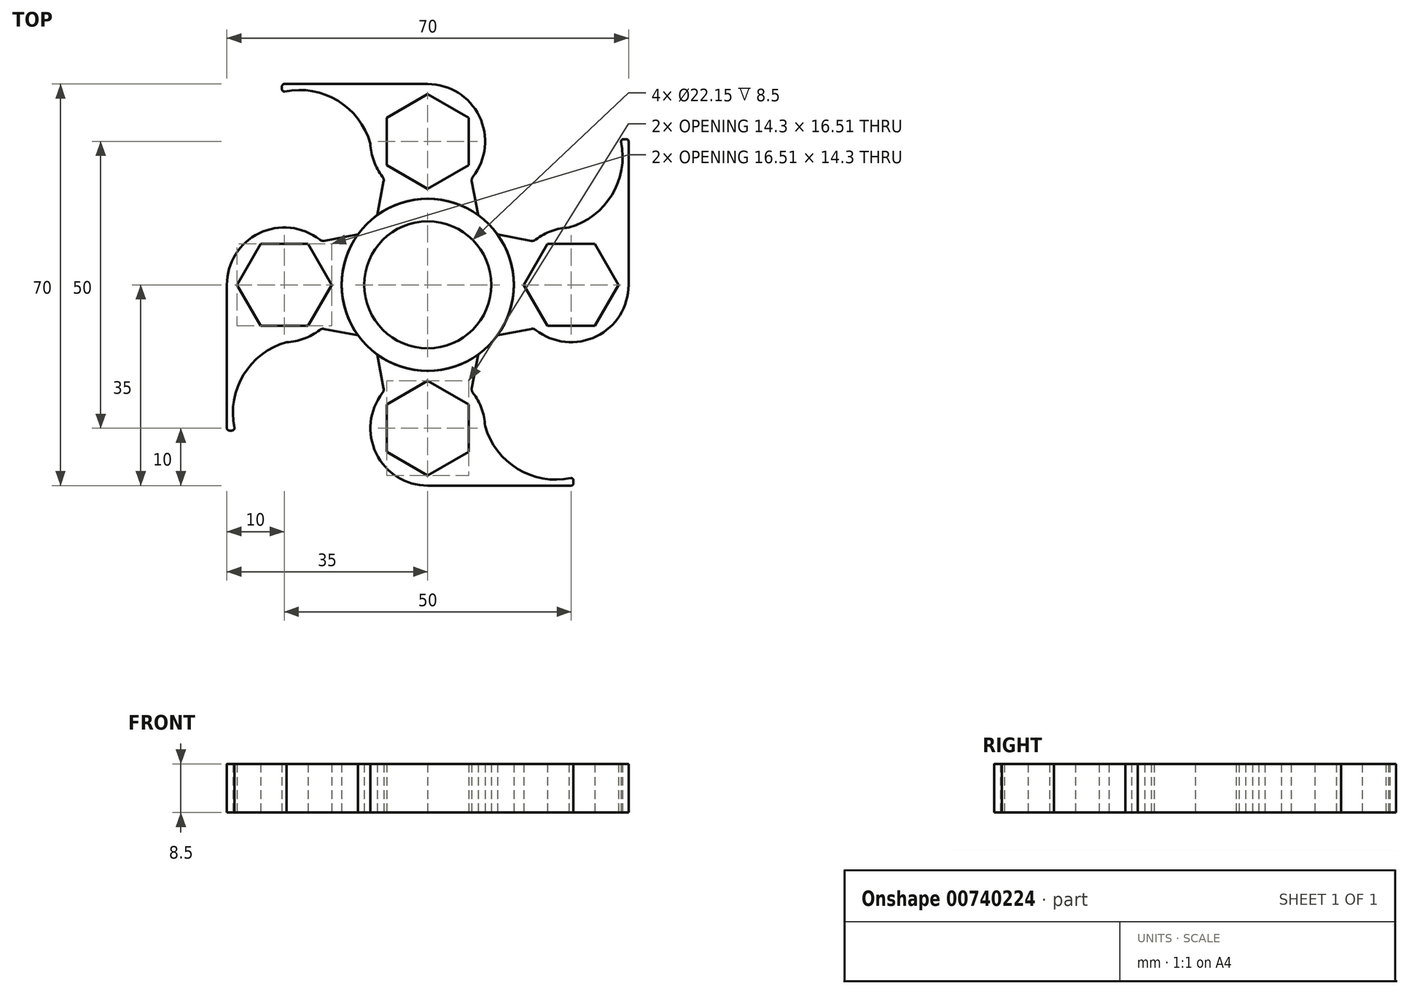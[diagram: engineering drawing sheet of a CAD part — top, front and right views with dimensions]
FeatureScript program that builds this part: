
annotation { "Feature Type Name" : "Feature", "Feature Type Description" : "" }
export const myFeature = defineFeature(function(context is Context, id is Id, definition is map)
    precondition{}
    {
        {
            var Q0;
            Q0=qCreatedBy(makeId("Top.planeOp"),FACE);
            var sketch = newSketch(context, id + "F0", { "sketchPlane" : qUnion([Q0])});
            skArc(sketch, "E0", {"start": v(-8.79, 12.16) * mm, "mid": v(0, -15) * mm, "end": v(8.79, 12.16) * mm});
            skCircle(sketch, "E1", {"center": v(0, 0) * mm, "radius": 11.07 * mm});
            skArc(sketch, "E2", {"start": v(7.88, 18.84) * mm, "mid": v(8.99, 29.38) * mm, "end": v(0, 35) * mm});
            skCircle(sketch, "E3.cCircle", {"center": v(0, 25) * mm, "radius": 7.15 * mm, "construction": true});
            skLineSegment(sketch, "E3.0", {"start": v(7.15, 29.13) * mm, "end": v(7.15, 20.87) * mm});
            skLineSegment(sketch, "E3.1", {"start": v(7.15, 20.87) * mm, "end": v(0, 16.74) * mm});
            skLineSegment(sketch, "E3.2", {"start": v(0, 16.74) * mm, "end": v(-7.15, 20.87) * mm});
            skLineSegment(sketch, "E3.3", {"start": v(-7.15, 20.87) * mm, "end": v(-7.15, 29.13) * mm});
            skLineSegment(sketch, "E3.4", {"start": v(-7.15, 29.13) * mm, "end": v(0, 33.26) * mm});
            skLineSegment(sketch, "E3.5", {"start": v(0, 33.26) * mm, "end": v(7.15, 29.13) * mm});
            skPoint(sketch, "E3.0.midPoint", {"position": v(7.15, 25) * mm});
            skLineSegment(sketch, "E4", {"start": v(0, 35) * mm, "end": v(-25, 35) * mm});
            skArc(sketch, "E5", {"start": v(-10, 24.61) * mm, "mid": v(-15.68, 32.08) * mm, "end": v(-24.92, 33.7) * mm});
            skLineSegment(sketch, "E6", {"start": v(11.07, 0) * mm, "end": v(7.68, 18.04) * mm, "construction": true});
            skLineSegment(sketch, "E7", {"start": v(-11.08, 0) * mm, "end": v(-7.68, 18.04) * mm, "construction": true});
            skLineSegment(sketch, "E8", {"start": v(8.79, 12.16) * mm, "end": v(7.6, 18.5) * mm});
            skLineSegment(sketch, "E9", {"start": v(-8.79, 12.16) * mm, "end": v(-7.6, 18.5) * mm});
            skArc(sketch, "E10.trimOffspring", {"start": v(-10, 24.61) * mm, "mid": v(-9.39, 21.56) * mm, "end": v(-7.88, 18.84) * mm});
            skLineSegment(sketch, "E11", {"start": v(-25.4, 34.6) * mm, "end": v(-25.4, 34.1) * mm});
            skPoint(sketch, "E12.visualSharp", {"position": v(-25.4, 33.6) * mm});
            skArc(sketch, "E12.filletArc", {"start": v(-25.4, 34.1) * mm, "mid": v(-25.25, 33.8) * mm, "end": v(-24.92, 33.7) * mm});
            skPoint(sketch, "E13.visualSharp", {"position": v(-25.4, 35) * mm});
            skArc(sketch, "E13.filletArc", {"start": v(-25, 35) * mm, "mid": v(-25.28, 34.88) * mm, "end": v(-25.4, 34.6) * mm});
            skPoint(sketch, "E14.visualSharp", {"position": v(-7.6, 18.5) * mm});
            skArc(sketch, "E14.filletArc", {"start": v(-7.68, 18.04) * mm, "mid": v(-7.7, 18.46) * mm, "end": v(-7.88, 18.84) * mm});
            skPoint(sketch, "E15.visualSharp", {"position": v(7.6, 18.5) * mm});
            skArc(sketch, "E15.filletArc", {"start": v(7.88, 18.84) * mm, "mid": v(7.7, 18.46) * mm, "end": v(7.68, 18.04) * mm});
            skSolve(sketch);
        }
        {
            var Q0;
            Q0=qCreatedBy(makeId("Right.planeOp"),FACE);
            var sketch = newSketch(context, id + "F1", { "sketchPlane" : qUnion([Q0])});
            skLineSegment(sketch, "E16", {"start": v(0, 0) * mm, "end": v(0, 33.36) * mm, "construction": true});
            skSolve(sketch);
        }
        {
            var Q0;
            Q0=makeQuery(id+"F0.imprint","IMPRINT",FACE,{"disambiguationData":[TD([[makeQuery(id+"F0.imprint","IMPRINT",EDGE,{"derivedFrom":sQuery(id+"F0.wireOp",EDGE,"E1")}),-1.0]])]});
            var Q1;
            Q1=makeQuery(id+"F0.imprint","IMPRINT",FACE,{"disambiguationData":[TD([[makeQuery(id+"F0.imprint","IMPRINT",EDGE,{"derivedFrom":sQuery(id+"F0.wireOp",EDGE,"12b2c2e4-33c8-48a8-a6f1-434ee54bed1e.1.0")}),1.0]])]});
            var Q2;
            Q2=makeQuery(id+"F0.imprint","IMPRINT",FACE,{"disambiguationData":[TD([[makeQuery(id+"F0.imprint","IMPRINT",EDGE,{"derivedFrom":sQuery(id+"F0.wireOp",EDGE,"12b2c2e4-33c8-48a8-a6f1-434ee54bed1e.2.0")}),1.0]])]});
            extrude(context, id + "F2", {"entities" : qUnion([Q0, Q1, Q2]), "depth" : 8.5 * mm, "offsetDistance" : 25 * mm});
        }
        {
            var Q0;
            Q0=makeQuery(id+"F2.opExtrude","SWEPT_BODY",BODY,{"disambiguationData":[OSD([sQuery(id+"F0.wireOp",EDGE,"E0"),sQuery(id+"F0.wireOp",EDGE,"E1"),sQuery(id+"F0.wireOp",EDGE,"E2"),sQuery(id+"F0.wireOp",EDGE,"E3.0"),sQuery(id+"F0.wireOp",EDGE,"E3.1"),sQuery(id+"F0.wireOp",EDGE,"E3.2"),sQuery(id+"F0.wireOp",EDGE,"E3.3"),sQuery(id+"F0.wireOp",EDGE,"E3.4"),sQuery(id+"F0.wireOp",EDGE,"E3.5"),sQuery(id+"F0.wireOp",EDGE,"E4"),sQuery(id+"F0.wireOp",EDGE,"E5"),sQuery(id+"F0.wireOp",EDGE,"E8"),sQuery(id+"F0.wireOp",EDGE,"E9"),sQuery(id+"F0.wireOp",EDGE,"E10.trimOffspring"),sQuery(id+"F0.wireOp",EDGE,"E11"),sQuery(id+"F0.wireOp",EDGE,"E12.filletArc"),sQuery(id+"F0.wireOp",EDGE,"E13.filletArc"),sQuery(id+"F0.wireOp",EDGE,"E14.filletArc"),sQuery(id+"F0.wireOp",EDGE,"E15.filletArc")])]});
            var Q1;
            Q1=sQuery(id+"F1.wireOp",EDGE,"E16");
            circularPattern(context, id + "F3", {"entities" : qUnion([Q0]), "axis" : qUnion([Q1]), "angle" : 360 * degree, "instanceCount" : 4, "equalSpace" : true});
        }
    });
